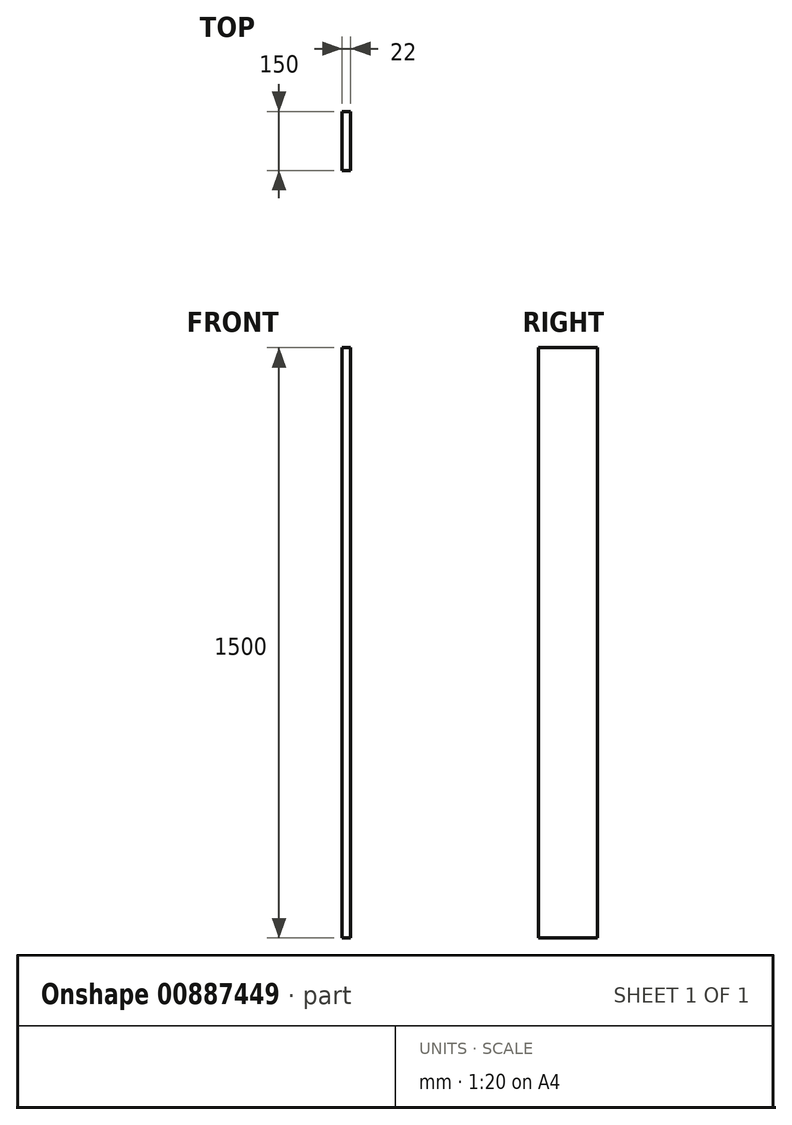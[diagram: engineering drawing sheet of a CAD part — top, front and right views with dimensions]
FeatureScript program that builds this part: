
annotation { "Feature Type Name" : "Feature", "Feature Type Description" : "" }
export const myFeature = defineFeature(function(context is Context, id is Id, definition is map)
    precondition{}
    {
        {
            var Q0;
            Q0=qCreatedBy(makeId("Right.planeOp"),FACE);
            var sketch = newSketch(context, id + "F0", { "sketchPlane" : qUnion([Q0])});
            skLineSegment(sketch, "E0.bottom", {"start": v(75, -750) * mm, "end": v(-75, -750) * mm});
            skLineSegment(sketch, "E0.top", {"start": v(75, 750) * mm, "end": v(-75, 750) * mm});
            skLineSegment(sketch, "E0.left", {"start": v(75, -750) * mm, "end": v(75, 750) * mm});
            skLineSegment(sketch, "E0.right", {"start": v(-75, -750) * mm, "end": v(-75, 750) * mm});
            skPoint(sketch, "E0.middle", {"position": v(0, 0) * mm});
            skSolve(sketch);
        }
        {
            var Q0;
            Q0=makeQuery(id+"F0.imprint","IMPRINT",FACE,{"disambiguationData":[TD([[makeQuery(id+"F0.imprint","IMPRINT",EDGE,{"derivedFrom":sQuery(id+"F0.wireOp",EDGE,"E0.bottom")}),-1.0]])]});
            extrude(context, id + "F1", {"entities" : qUnion([Q0]), "depth" : 22 * mm, "offsetDistance" : 25 * mm});
        }
    });
